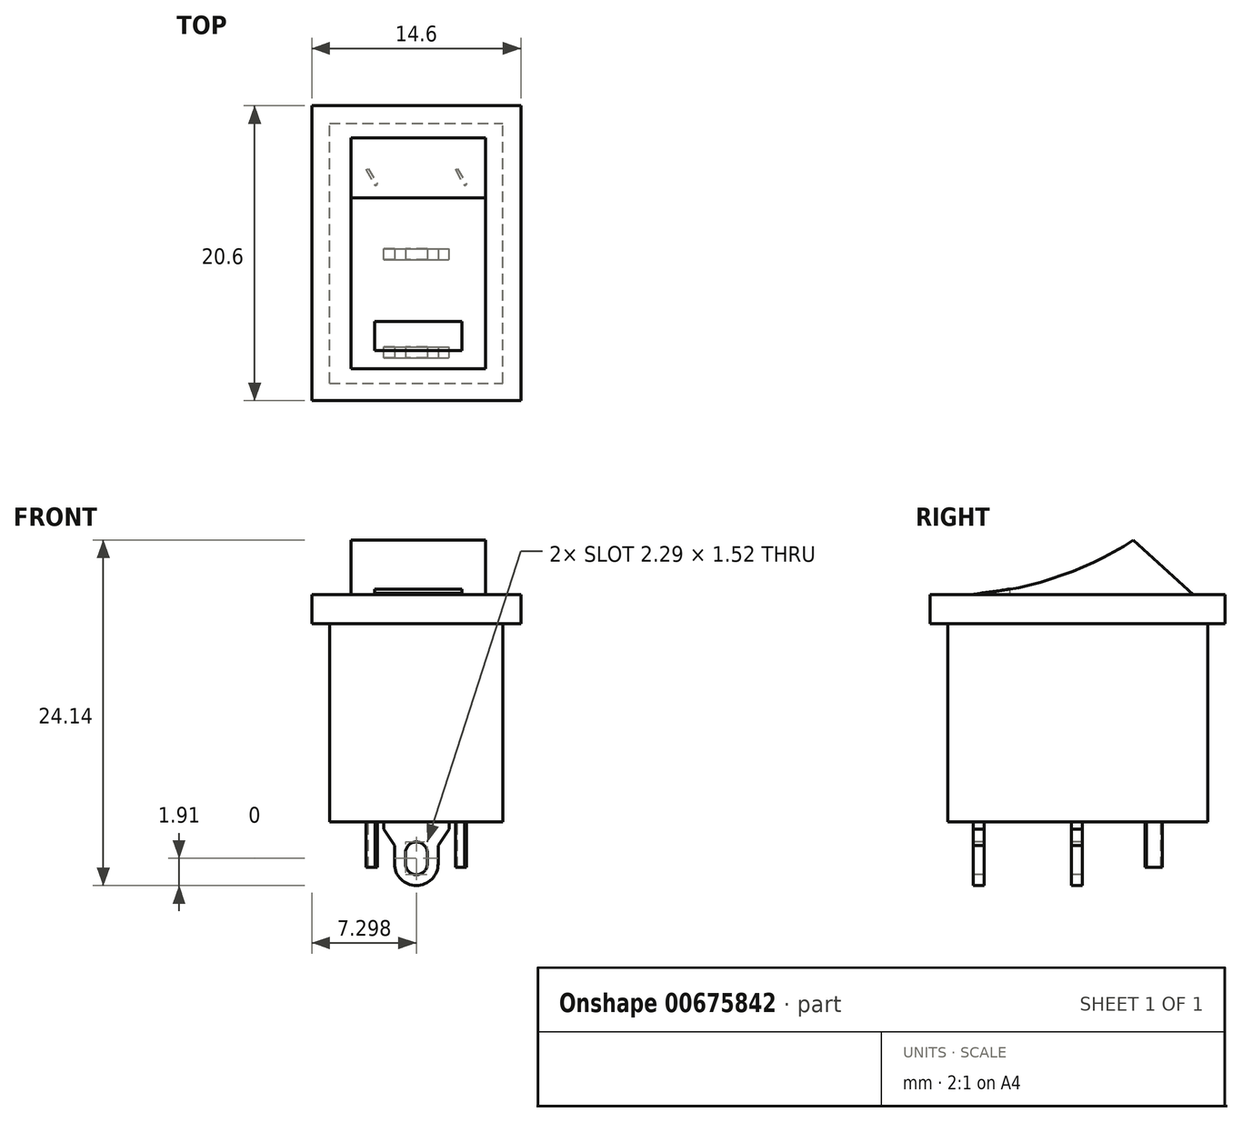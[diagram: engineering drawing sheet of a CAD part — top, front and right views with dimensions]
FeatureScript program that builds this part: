
annotation { "Feature Type Name" : "Feature", "Feature Type Description" : "" }
export const myFeature = defineFeature(function(context is Context, id is Id, definition is map)
    precondition{}
    {
        {
            var Q0;
            Q0=qCreatedBy(makeId("Top.planeOp"),FACE);
            var sketch = newSketch(context, id + "F0", { "sketchPlane" : qUnion([Q0])});
            skLineSegment(sketch, "E0.bottom", {"start": v(0, 0) * mm, "end": v(12.12, 0) * mm});
            skLineSegment(sketch, "E0.top", {"start": v(0, 18.16) * mm, "end": v(12.12, 18.16) * mm});
            skLineSegment(sketch, "E0.left", {"start": v(0, 0) * mm, "end": v(0, 18.16) * mm});
            skLineSegment(sketch, "E0.right", {"start": v(12.12, 0) * mm, "end": v(12.12, 18.16) * mm});
            skSolve(sketch);
        }
        {
            var Q0;
            Q0 = qSketchRegion(id + "F0", true);
            extrude(context, id + "F1", {"entities" : qUnion([Q0]), "depth" : 13.84 * mm, "offsetDistance" : 25.4 * mm});
        }
        {
            var Q0;
            Q0=makeQuery(id+"F1.opExtrude","CAP_FACE",FACE,{"disambiguationData":[OSD([sQuery(id+"F0.wireOp",EDGE,"E0.bottom"),sQuery(id+"F0.wireOp",EDGE,"E0.top"),sQuery(id+"F0.wireOp",EDGE,"E0.left"),sQuery(id+"F0.wireOp",EDGE,"E0.right")])],"isStart":false});
            var sketch = newSketch(context, id + "F2", { "sketchPlane" : qUnion([Q0])});
            skLineSegment(sketch, "E1.bottom", {"start": v(-1.24, 19.38) * mm, "end": v(13.36, 19.38) * mm});
            skLineSegment(sketch, "E1.top", {"start": v(-1.24, -1.22) * mm, "end": v(13.36, -1.22) * mm});
            skLineSegment(sketch, "E1.left", {"start": v(-1.24, 19.38) * mm, "end": v(-1.24, -1.22) * mm});
            skLineSegment(sketch, "E1.right", {"start": v(13.36, 19.38) * mm, "end": v(13.36, -1.22) * mm});
            skLineSegment(sketch, "E2", {"start": v(6.06, 19.38) * mm, "end": v(6.06, 18.16) * mm, "construction": true});
            skLineSegment(sketch, "E3", {"start": v(-1.24, 9.08) * mm, "end": v(0, 9.08) * mm, "construction": true});
            skSolve(sketch);
        }
        {
            var Q0;
            Q0 = qSketchRegion(id + "F2", true);
            extrude(context, id + "F3", {"entities" : qUnion([Q0]), "operationType" : NewBodyOperationType.ADD, "depth" : 2.03 * mm, "offsetDistance" : 25.4 * mm});
        }
        {
            var Q0;
            Q0=makeQuery(id+"F3.opExtrude","SWEPT_FACE",FACE,{"disambiguationData":[OSD([sQuery(id+"F2.wireOp",EDGE,"E1.right")])]});
            cPlane(context, id + "F4", {"entities" : qUnion([Q0]), "cplaneType" : CPlaneType.OFFSET, "offset" : 2.46 * mm, "oppositeDirection" : true, "width" : 152.4 * mm, "height" : 152.4 * mm});
        }
        {
            var Q0;
            Q0=qCreatedBy(id+"F4.planeOp",FACE);
            var sketch = newSketch(context, id + "F5", { "sketchPlane" : qUnion([Q0])});
            skArc(sketch, "E4", {"start": v(1.02, 15.88) * mm, "mid": v(7.24, 16.98) * mm, "end": v(12.95, 19.69) * mm});
            skLineSegment(sketch, "E5", {"start": v(12.95, 19.69) * mm, "end": v(17.15, 15.87) * mm});
            skLineSegment(sketch, "E6", {"start": v(17.14, 15.88) * mm, "end": v(1.02, 15.88) * mm});
            skSolve(sketch);
        }
        {
            var Q0;
            Q0 = qSketchRegion(id + "F5", true);
            extrude(context, id + "F6", {"entities" : qUnion([Q0]), "operationType" : NewBodyOperationType.ADD, "oppositeDirection" : true, "depth" : 9.4 * mm, "offsetDistance" : 25.4 * mm});
        }
        {
            var Q0;
            Q0=makeQuery(id+"F3.opExtrude","CAP_FACE",FACE,{"disambiguationData":[OSD([sQuery(id+"F2.wireOp",EDGE,"E1.bottom"),sQuery(id+"F2.wireOp",EDGE,"E1.top"),sQuery(id+"F2.wireOp",EDGE,"E1.left"),sQuery(id+"F2.wireOp",EDGE,"E1.right")])],"isStart":false});
            var sketch = newSketch(context, id + "F7", { "sketchPlane" : qUnion([Q0])});
            skLineSegment(sketch, "E7.bottom", {"start": v(3.15, 4.32) * mm, "end": v(9.25, 4.32) * mm});
            skLineSegment(sketch, "E7.top", {"start": v(3.15, 2.29) * mm, "end": v(9.25, 2.29) * mm});
            skLineSegment(sketch, "E7.left", {"start": v(3.15, 4.32) * mm, "end": v(3.15, 2.29) * mm});
            skLineSegment(sketch, "E7.right", {"start": v(9.25, 4.32) * mm, "end": v(9.25, 2.29) * mm});
            skLineSegment(sketch, "E8", {"start": v(6.2, 1.02) * mm, "end": v(6.2, 2.29) * mm, "construction": true});
            skSolve(sketch);
        }
        {
            var Q0;
            Q0 = qSketchRegion(id + "F7", true);
            var Q1;
            Q1 = qConstructionFilter(qBodyType(qCreatedBy(id + "F7" ,EDGE), BodyType.WIRE), ConstructionObject.NO);
            extrude(context, id + "F8", {"entities" : qUnion([Q0]), "surfaceEntities" : qUnion([Q1]), "endBound" : BoundingType.UP_TO_NEXT, "depth" : 0.38 * mm, "hasOffset" : true, "offsetDistance" : 0.03 * mm, "offsetOppositeDirection" : true});
        }
        {
            var Q0;
            Q0=makeQuery(id+"F1.opExtrude","CAP_FACE",FACE,{"disambiguationData":[OSD([sQuery(id+"F0.wireOp",EDGE,"E0.bottom"),sQuery(id+"F0.wireOp",EDGE,"E0.top"),sQuery(id+"F0.wireOp",EDGE,"E0.left"),sQuery(id+"F0.wireOp",EDGE,"E0.right")])],"isStart":true});
            var sketch = newSketch(context, id + "F9", { "sketchPlane" : qUnion([Q0])});
            skLineSegment(sketch, "E9.bottom", {"start": v(3.77, -1.78) * mm, "end": v(8.34, -1.78) * mm});
            skLineSegment(sketch, "E9.top", {"start": v(3.77, -2.54) * mm, "end": v(8.34, -2.54) * mm});
            skLineSegment(sketch, "E9.left", {"start": v(3.77, -1.78) * mm, "end": v(3.77, -2.54) * mm});
            skLineSegment(sketch, "E9.right", {"start": v(8.34, -1.78) * mm, "end": v(8.34, -2.54) * mm});
            skLineSegment(sketch, "E10.bottom", {"start": v(3.77, -8.64) * mm, "end": v(8.34, -8.64) * mm});
            skLineSegment(sketch, "E10.top", {"start": v(3.77, -9.4) * mm, "end": v(8.34, -9.4) * mm});
            skLineSegment(sketch, "E10.left", {"start": v(3.77, -8.64) * mm, "end": v(3.77, -9.4) * mm});
            skLineSegment(sketch, "E10.right", {"start": v(8.34, -8.64) * mm, "end": v(8.34, -9.4) * mm});
            skLineSegment(sketch, "E11", {"start": v(6.06, 0) * mm, "end": v(6.06, -1.78) * mm, "construction": true});
            skLineSegment(sketch, "E12.bottom", {"start": v(2.54, -14.9) * mm, "end": v(2.7, -14.99) * mm});
            skLineSegment(sketch, "E12.top", {"start": v(3.18, -13.8) * mm, "end": v(3.33, -13.89) * mm});
            skLineSegment(sketch, "E12.left", {"start": v(2.54, -14.9) * mm, "end": v(3.18, -13.8) * mm});
            skLineSegment(sketch, "E12.right", {"start": v(2.7, -14.99) * mm, "end": v(3.33, -13.89) * mm});
            skLineSegment(sketch, "E13.bottom", {"start": v(8.79, -14.9) * mm, "end": v(8.94, -14.99) * mm});
            skLineSegment(sketch, "E13.top", {"start": v(9.42, -13.8) * mm, "end": v(9.58, -13.89) * mm});
            skLineSegment(sketch, "E13.left", {"start": v(8.79, -14.9) * mm, "end": v(9.42, -13.8) * mm});
            skLineSegment(sketch, "E13.right", {"start": v(8.94, -14.99) * mm, "end": v(9.58, -13.89) * mm});
            skSolve(sketch);
        }
        {
            var Q0;
            Q0 = qSketchRegion(id + "F9", true);
            extrude(context, id + "F10", {"entities" : qUnion([Q0]), "operationType" : NewBodyOperationType.ADD, "depth" : 3.17 * mm, "offsetDistance" : 25.4 * mm});
        }
        {
            var Q0;
            Q0=makeQuery(id+"F10.opExtrude","CAP_FACE",FACE,{"disambiguationData":[OSD([sQuery(id+"F9.wireOp",EDGE,"E9.bottom"),sQuery(id+"F9.wireOp",EDGE,"E9.top"),sQuery(id+"F9.wireOp",EDGE,"E9.left"),sQuery(id+"F9.wireOp",EDGE,"E9.right")])],"isStart":false});
            var sketch = newSketch(context, id + "F11", { "sketchPlane" : qUnion([Q0])});
            skLineSegment(sketch, "E14.0.0", {"start": v(3.77, -1.78) * mm, "end": v(3.77, -2.54) * mm});
            skLineSegment(sketch, "E14.0.1", {"start": v(3.77, -2.54) * mm, "end": v(8.34, -2.54) * mm});
            skLineSegment(sketch, "E14.0.2", {"start": v(8.34, -2.54) * mm, "end": v(8.34, -1.78) * mm});
            skLineSegment(sketch, "E14.0.3", {"start": v(8.34, -1.78) * mm, "end": v(3.77, -1.78) * mm});
            skLineSegment(sketch, "E15.0.0", {"start": v(3.77, -8.64) * mm, "end": v(3.77, -9.4) * mm});
            skLineSegment(sketch, "E15.0.1", {"start": v(3.77, -9.4) * mm, "end": v(8.34, -9.4) * mm});
            skLineSegment(sketch, "E15.0.2", {"start": v(8.34, -9.4) * mm, "end": v(8.34, -8.64) * mm});
            skLineSegment(sketch, "E15.0.3", {"start": v(8.34, -8.64) * mm, "end": v(3.77, -8.64) * mm});
            skSolve(sketch);
        }
        {
            var Q0;
            Q0 = qSketchRegion(id + "F11", true);
            extrude(context, id + "F12", {"entities" : qUnion([Q0]), "operationType" : NewBodyOperationType.ADD, "depth" : 1.27 * mm, "offsetDistance" : 25.4 * mm});
        }
        {
            var Q0;
            Q0=makeQuery(id+"F12.boolean.opBoolean","MERGE",FACE,{"derivedFrom":[makeQuery(id+"F10.opExtrude","SWEPT_FACE",FACE,{"disambiguationData":[OSD([sQuery(id+"F9.wireOp",EDGE,"E9.bottom")])]}),makeQuery(id+"F12.opExtrude","SWEPT_FACE",FACE,{"disambiguationData":[OSD([sQuery(id+"F11.wireOp",EDGE,"E14.0.3")])]})]});
            var sketch = newSketch(context, id + "F13", { "sketchPlane" : qUnion([Q0])});
            skArc(sketch, "E16", {"start": v(4.53, -2.92) * mm, "mid": v(6.06, -4.45) * mm, "end": v(7.58, -2.92) * mm});
            skLineSegment(sketch, "E17", {"start": v(6.06, 0) * mm, "end": v(6.06, -4.45) * mm, "construction": true});
            skLineSegment(sketch, "E18", {"start": v(7.58, -2.92) * mm, "end": v(7.58, -1.65) * mm});
            skLineSegment(sketch, "E19", {"start": v(4.53, -2.92) * mm, "end": v(4.53, -1.65) * mm});
            skLineSegment(sketch, "E20", {"start": v(4.53, -1.65) * mm, "end": v(3.77, -0.5) * mm});
            skLineSegment(sketch, "E21", {"start": v(7.58, -1.65) * mm, "end": v(8.34, -0.5) * mm});
            skLineSegment(sketch, "E22", {"start": v(3.77, -0.5) * mm, "end": v(3.77, -4.45) * mm});
            skLineSegment(sketch, "E23", {"start": v(3.77, -4.45) * mm, "end": v(8.34, -4.45) * mm});
            skLineSegment(sketch, "E24", {"start": v(8.34, -4.45) * mm, "end": v(8.34, -0.5) * mm});
            skSolve(sketch);
        }
        {
            var Q0;
            Q0 = qSketchRegion(id + "F13", true);
            extrude(context, id + "F14", {"entities" : qUnion([Q0]), "operationType" : NewBodyOperationType.REMOVE, "endBound" : BoundingType.THROUGH_ALL, "oppositeDirection" : true, "depth" : 25.4 * mm, "offsetDistance" : 25.4 * mm});
        }
        {
            var Q0;
            Q0=makeQuery(id+"F12.boolean.opBoolean","MERGE",FACE,{"derivedFrom":[makeQuery(id+"F10.opExtrude","SWEPT_FACE",FACE,{"disambiguationData":[OSD([sQuery(id+"F9.wireOp",EDGE,"E9.bottom")])]}),makeQuery(id+"F12.opExtrude","SWEPT_FACE",FACE,{"disambiguationData":[OSD([sQuery(id+"F11.wireOp",EDGE,"E14.0.3")])]})]});
            var sketch = newSketch(context, id + "F15", { "sketchPlane" : qUnion([Q0])});
            skArc(sketch, "E25", {"start": v(5.3, -2.92) * mm, "mid": v(6.06, -3.68) * mm, "end": v(6.82, -2.92) * mm});
            skArc(sketch, "E26", {"start": v(6.82, -2.16) * mm, "mid": v(6.06, -1.4) * mm, "end": v(5.3, -2.16) * mm});
            skLineSegment(sketch, "E27", {"start": v(5.3, -2.16) * mm, "end": v(5.3, -2.92) * mm});
            skLineSegment(sketch, "E28", {"start": v(6.82, -2.16) * mm, "end": v(6.82, -2.92) * mm});
            skSolve(sketch);
        }
        {
            var Q0;
            Q0 = qSketchRegion(id + "F15", true);
            extrude(context, id + "F16", {"entities" : qUnion([Q0]), "operationType" : NewBodyOperationType.REMOVE, "endBound" : BoundingType.THROUGH_ALL, "oppositeDirection" : true, "depth" : 25.4 * mm, "offsetDistance" : 25.4 * mm});
        }
    });
